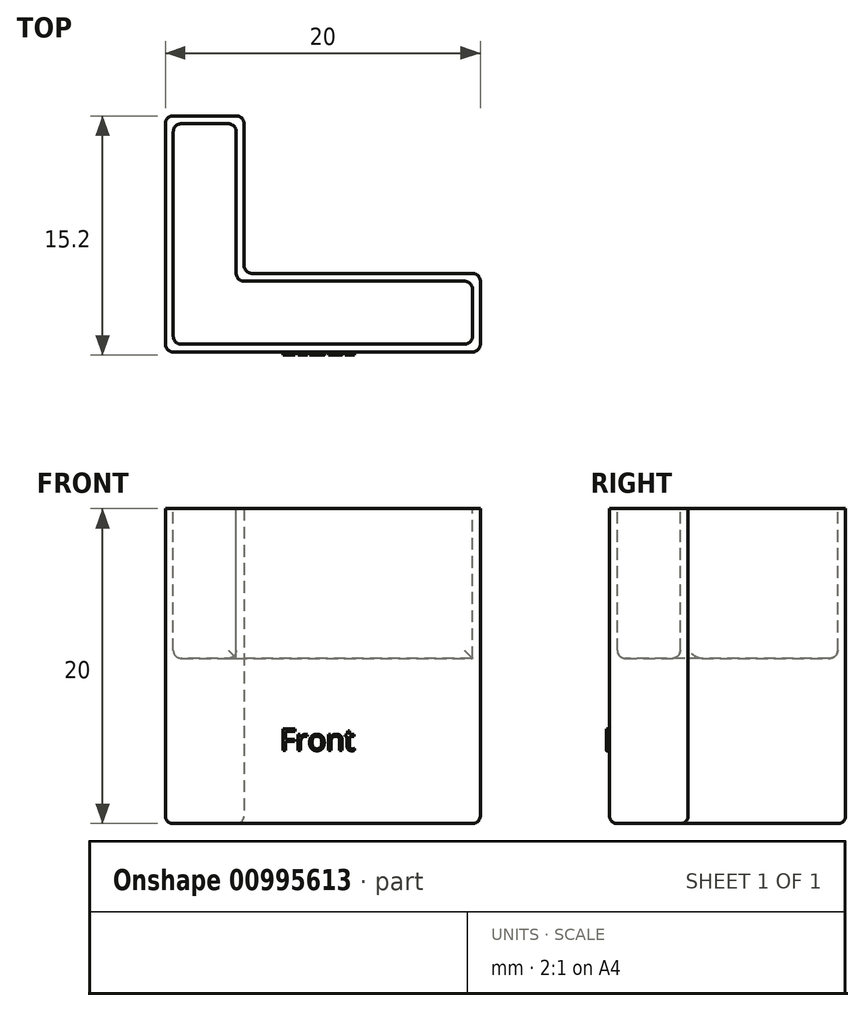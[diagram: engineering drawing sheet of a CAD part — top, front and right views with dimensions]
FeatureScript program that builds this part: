
annotation { "Feature Type Name" : "Feature", "Feature Type Description" : "" }
export const myFeature = defineFeature(function(context is Context, id is Id, definition is map)
    precondition{}
    {
        {
            var Q0;
            Q0=qCreatedBy(makeId("Top.planeOp"),FACE);
            var sketch = newSketch(context, id + "F0", { "sketchPlane" : qUnion([Q0])});
            skLineSegment(sketch, "E0", {"start": v(0, 0) * mm, "end": v(-20, 0) * mm});
            skLineSegment(sketch, "E1", {"start": v(-20, 0) * mm, "end": v(-20, 15) * mm});
            skLineSegment(sketch, "E2", {"start": v(-20, 15) * mm, "end": v(-15, 15) * mm});
            skLineSegment(sketch, "E3", {"start": v(-15, 15) * mm, "end": v(-15, 5) * mm});
            skLineSegment(sketch, "E4", {"start": v(-15, 5) * mm, "end": v(0, 5) * mm});
            skLineSegment(sketch, "E5", {"start": v(0, 5) * mm, "end": v(0, 0) * mm});
            skSolve(sketch);
        }
        {
            var Q0;
            Q0 = qSketchRegion(id + "F0", true);
            extrude(context, id + "F1", {"entities" : qUnion([Q0]), "depth" : 20 * mm, "offsetDistance" : 25 * mm});
        }
        {
            var Q0;
            Q0=makeQuery(id+"F1.opExtrude","CAP_FACE",FACE,{"disambiguationData":[OSD([sQuery(id+"F0.wireOp",EDGE,"E0"),sQuery(id+"F0.wireOp",EDGE,"E1"),sQuery(id+"F0.wireOp",EDGE,"E2"),sQuery(id+"F0.wireOp",EDGE,"E3"),sQuery(id+"F0.wireOp",EDGE,"E4"),sQuery(id+"F0.wireOp",EDGE,"E5")])],"isStart":false});
            var sketch = newSketch(context, id + "F2", { "sketchPlane" : qUnion([Q0])});
            skLineSegment(sketch, "E6", {"start": v(-19.5, 14.5) * mm, "end": v(-19.5, 0.5) * mm});
            skLineSegment(sketch, "E7", {"start": v(-19.5, 0.5) * mm, "end": v(-0.5, 0.5) * mm});
            skLineSegment(sketch, "E8", {"start": v(-0.5, 0.5) * mm, "end": v(-0.5, 4.5) * mm});
            skLineSegment(sketch, "E9", {"start": v(-0.5, 4.5) * mm, "end": v(-15.5, 4.5) * mm});
            skLineSegment(sketch, "E10", {"start": v(-15.5, 4.5) * mm, "end": v(-15.5, 14.5) * mm});
            skLineSegment(sketch, "E11", {"start": v(-15.5, 14.5) * mm, "end": v(-19.5, 14.5) * mm});
            skSolve(sketch);
        }
        {
            var Q0;
            Q0 = qSketchRegion(id + "F2", true);
            extrude(context, id + "F3", {"entities" : qUnion([Q0]), "operationType" : NewBodyOperationType.REMOVE, "oppositeDirection" : true, "depth" : 9.5 * mm, "offsetDistance" : 25 * mm});
        }
        {
            var Q0;
            Q0=makeQuery(id+"F3.boolean.opBoolean","COPY",EDGE,{"derivedFrom":makeQuery(id+"F3.opExtrude","SWEPT_EDGE",EDGE,{"disambiguationData":[OSD([sQuery(id+"F2.wireOp",EDGE,"E6"),sQuery(id+"F2.wireOp",EDGE,"E7")])]})});
            var Q1;
            Q1=makeQuery(id+"F1.opExtrude","SWEPT_EDGE",EDGE,{"disambiguationData":[OSD([sQuery(id+"F0.wireOp",EDGE,"E3"),sQuery(id+"F0.wireOp",EDGE,"E4")])]});
            var Q2;
            Q2=makeQuery(id+"F3.boolean.opBoolean","COPY",EDGE,{"derivedFrom":makeQuery(id+"F3.opExtrude","SWEPT_EDGE",EDGE,{"disambiguationData":[OSD([sQuery(id+"F2.wireOp",EDGE,"E7"),sQuery(id+"F2.wireOp",EDGE,"E8")])]})});
            var Q3;
            Q3=makeQuery(id+"F3.boolean.opBoolean","COPY",EDGE,{"derivedFrom":makeQuery(id+"F3.opExtrude","SWEPT_EDGE",EDGE,{"disambiguationData":[OSD([sQuery(id+"F2.wireOp",EDGE,"E8"),sQuery(id+"F2.wireOp",EDGE,"E9")])]})});
            var Q4;
            Q4=makeQuery(id+"F3.boolean.opBoolean","COPY",EDGE,{"derivedFrom":makeQuery(id+"F3.opExtrude","SWEPT_EDGE",EDGE,{"disambiguationData":[OSD([sQuery(id+"F2.wireOp",EDGE,"E9"),sQuery(id+"F2.wireOp",EDGE,"E10")])]})});
            var Q5;
            Q5=makeQuery(id+"F1.opExtrude","SWEPT_EDGE",EDGE,{"disambiguationData":[OSD([sQuery(id+"F0.wireOp",EDGE,"E0"),sQuery(id+"F0.wireOp",EDGE,"E1")])]});
            var Q6;
            Q6=makeQuery(id+"F3.boolean.opBoolean","COPY",EDGE,{"derivedFrom":makeQuery(id+"F3.opExtrude","SWEPT_EDGE",EDGE,{"disambiguationData":[OSD([sQuery(id+"F2.wireOp",EDGE,"E6"),sQuery(id+"F2.wireOp",EDGE,"E11")])]})});
            var Q7;
            Q7=makeQuery(id+"F3.boolean.opBoolean","COPY",EDGE,{"derivedFrom":makeQuery(id+"F3.opExtrude","CAP_EDGE",EDGE,{"disambiguationData":[OSD([sQuery(id+"F2.wireOp",EDGE,"E6")])],"isStart":false})});
            var Q8;
            Q8=makeQuery(id+"F3.boolean.opBoolean","COPY",EDGE,{"derivedFrom":makeQuery(id+"F3.opExtrude","CAP_EDGE",EDGE,{"disambiguationData":[OSD([sQuery(id+"F2.wireOp",EDGE,"E11")])],"isStart":false})});
            var Q9;
            Q9=makeQuery(id+"F3.boolean.opBoolean","COPY",EDGE,{"derivedFrom":makeQuery(id+"F3.opExtrude","SWEPT_EDGE",EDGE,{"disambiguationData":[OSD([sQuery(id+"F2.wireOp",EDGE,"E10"),sQuery(id+"F2.wireOp",EDGE,"E11")])]})});
            var Q10;
            Q10=makeQuery(id+"F3.boolean.opBoolean","COPY",EDGE,{"derivedFrom":makeQuery(id+"F3.opExtrude","CAP_EDGE",EDGE,{"disambiguationData":[OSD([sQuery(id+"F2.wireOp",EDGE,"E9")])],"isStart":false})});
            var Q11;
            Q11=makeQuery(id+"F3.boolean.opBoolean","COPY",EDGE,{"derivedFrom":makeQuery(id+"F3.opExtrude","CAP_EDGE",EDGE,{"disambiguationData":[OSD([sQuery(id+"F2.wireOp",EDGE,"E7")])],"isStart":false})});
            var Q12;
            Q12=makeQuery(id+"F1.opExtrude","SWEPT_EDGE",EDGE,{"disambiguationData":[OSD([sQuery(id+"F0.wireOp",EDGE,"E4"),sQuery(id+"F0.wireOp",EDGE,"E5")])]});
            var Q13;
            Q13=makeQuery(id+"F1.opExtrude","SWEPT_EDGE",EDGE,{"disambiguationData":[OSD([sQuery(id+"F0.wireOp",EDGE,"E0"),sQuery(id+"F0.wireOp",EDGE,"E5")])]});
            var Q14;
            Q14=makeQuery(id+"F1.opExtrude","SWEPT_EDGE",EDGE,{"disambiguationData":[OSD([sQuery(id+"F0.wireOp",EDGE,"E2"),sQuery(id+"F0.wireOp",EDGE,"E3")])]});
            var Q15;
            Q15=makeQuery(id+"F1.opExtrude","SWEPT_EDGE",EDGE,{"disambiguationData":[OSD([sQuery(id+"F0.wireOp",EDGE,"E1"),sQuery(id+"F0.wireOp",EDGE,"E2")])]});
            var Q16;
            Q16=makeQuery(id+"F1.opExtrude","CAP_EDGE",EDGE,{"disambiguationData":[OSD([sQuery(id+"F0.wireOp",EDGE,"E4")])],"isStart":true});
            var Q17;
            Q17=makeQuery(id+"F1.opExtrude","CAP_EDGE",EDGE,{"disambiguationData":[OSD([sQuery(id+"F0.wireOp",EDGE,"E3")])],"isStart":true});
            var Q18;
            Q18=makeQuery(id+"F1.opExtrude","CAP_EDGE",EDGE,{"disambiguationData":[OSD([sQuery(id+"F0.wireOp",EDGE,"E5")])],"isStart":true});
            var Q19;
            Q19=makeQuery(id+"F1.opExtrude","CAP_EDGE",EDGE,{"disambiguationData":[OSD([sQuery(id+"F0.wireOp",EDGE,"E0")])],"isStart":true});
            var Q20;
            Q20=makeQuery(id+"F1.opExtrude","CAP_EDGE",EDGE,{"disambiguationData":[OSD([sQuery(id+"F0.wireOp",EDGE,"E1")])],"isStart":true});
            var Q21;
            Q21=makeQuery(id+"F1.opExtrude","CAP_EDGE",EDGE,{"disambiguationData":[OSD([sQuery(id+"F0.wireOp",EDGE,"E2")])],"isStart":true});
            fillet(context, id + "F4", {"entities" : qUnion([Q0, Q1, Q2, Q3, Q4, Q5, Q6, Q7, Q8, Q9, Q10, Q11, Q12, Q13, Q14, Q15, Q16, Q17, Q18, Q19, Q20, Q21]), "radius" : 0.5 * mm, "tangentPropagation" : true, "allowEdgeOverflow" : false});
        }
        {
            var Q0;
            Q0=makeQuery(id+"F1.opExtrude","SWEPT_FACE",FACE,{"disambiguationData":[OSD([sQuery(id+"F0.wireOp",EDGE,"E0")])]});
            var sketch = newSketch(context, id + "F5", { "sketchPlane" : qUnion([Q0])});
            skText(sketch, "E12", { "text": "Front", "fontName": "OpenSans-Regular.ttf"});
            const initialGuessF5  = {"E12": [-0.01271, 0.00464, 1, 0, 0.00137]};
            skSetInitialGuess(sketch, initialGuessF5);
            skSolve(sketch);
        }
        {
            var Q0;
            Q0 = qSketchRegion(id + "F5", true);
            extrude(context, id + "F6", {"entities" : qUnion([Q0]), "operationType" : NewBodyOperationType.ADD, "depth" : 0.2 * mm, "offsetDistance" : 25 * mm});
        }
    });
